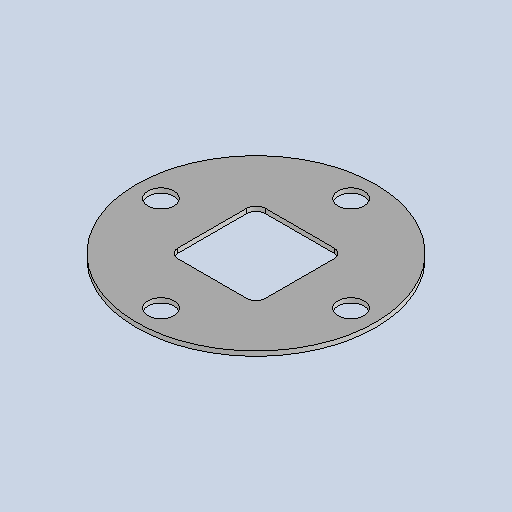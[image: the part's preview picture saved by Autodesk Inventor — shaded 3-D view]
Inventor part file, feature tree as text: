
AUTODESK INVENTOR PART (.ipt)
format: ipt  version: 2025.1 (Build 291241020, 241B)  size: 226,304 bytes
history: native  units: mm
features: other x3, sketch x2, sheet_metal_op x1, pattern_circular x1, chamfer x1
ambient origin geometry x8: Origin, YZ Plane, XZ Plane, XY Plane, X Axis, Y Axis, Z Axis, Center Point
bodies: Body1 (feature_tree)
feature tree (8):
  sheet_metal_op  "Face3"
  pattern_circular  "Circular Pattern1"  Count=50  [1 undecoded]
  chamfer  "Corner Round1"
  sketch  "Sketch1"  dims[d156=3.0mm]
  other  "Plate5"
  sketch  "Sketch7"  dims[d157=156.0mm d158=57.0mm d159=57.0mm d160=17.0mm d161=62.0mm d162=3.0mm d163=0.0mm d164=40.0mm d165=360.0deg d170=6.0mm]
  other  "Cut1"
  other  "Definition1"
note: 1 required parameter value undecoded (feature->parameter linkage not recoverable at this tier; creation-order binding heuristic only, values carry confidence <= 0.55)
